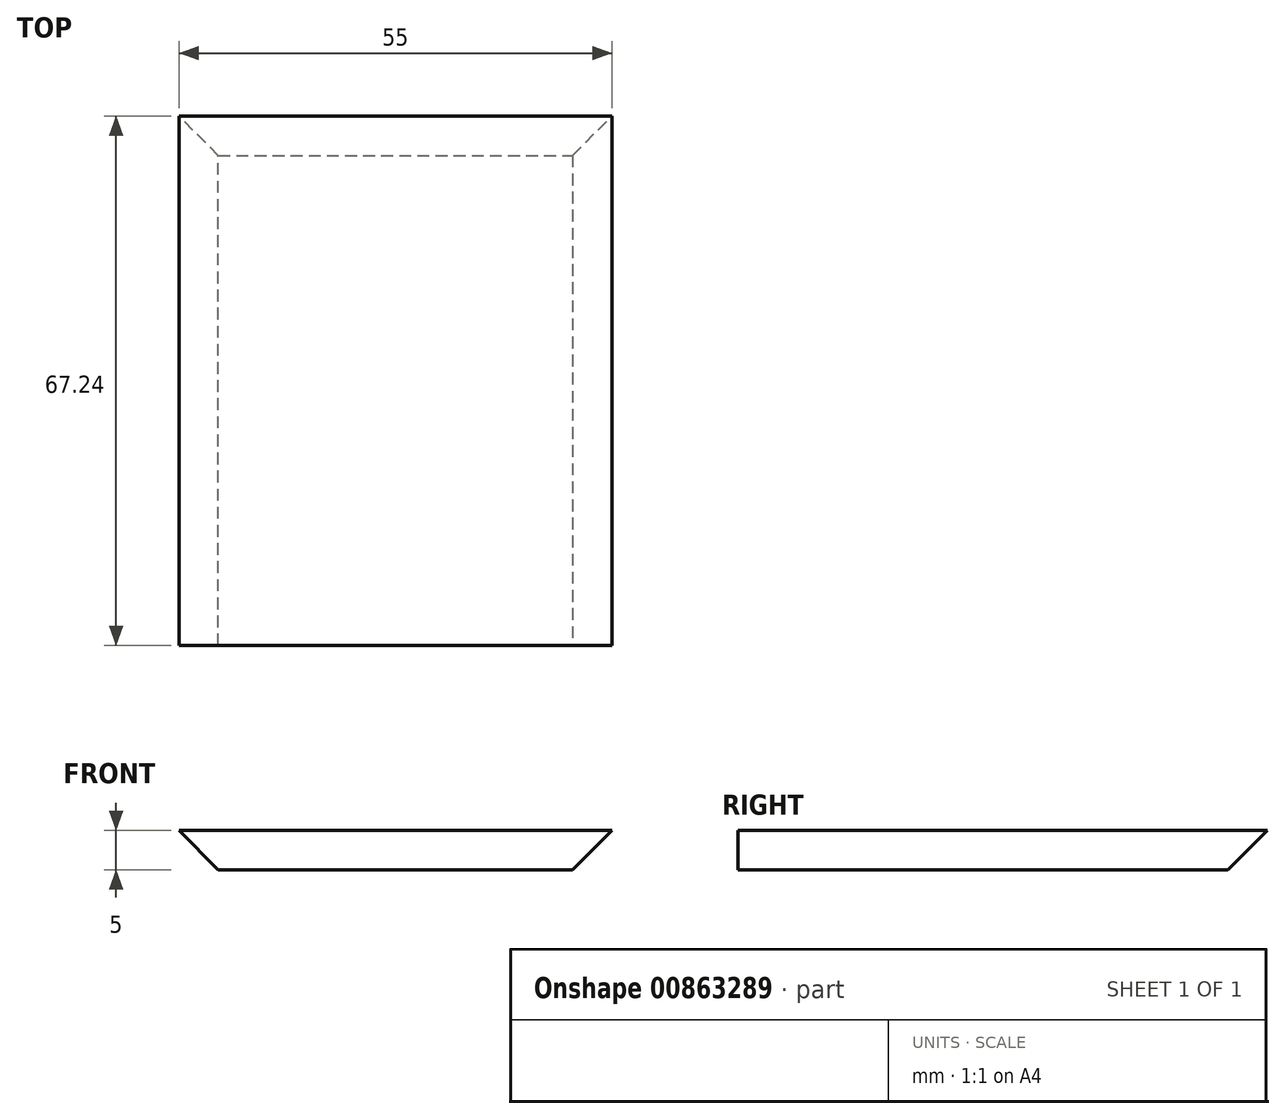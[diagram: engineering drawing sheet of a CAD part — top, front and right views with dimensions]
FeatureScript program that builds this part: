
annotation { "Feature Type Name" : "Feature", "Feature Type Description" : "" }
export const myFeature = defineFeature(function(context is Context, id is Id, definition is map)
    precondition{}
    {
        {
            var Q0;
            Q0=qCreatedBy(makeId("Top.planeOp"),FACE);
            var sketch = newSketch(context, id + "F0", { "sketchPlane" : qUnion([Q0])});
            skLineSegment(sketch, "E0.bottom", {"start": v(27.5, -52.5) * mm, "end": v(-27.5, -52.5) * mm});
            skLineSegment(sketch, "E0.top", {"start": v(27.5, 52.5) * mm, "end": v(-27.5, 52.5) * mm});
            skLineSegment(sketch, "E0.left", {"start": v(27.5, -52.5) * mm, "end": v(27.5, 52.5) * mm});
            skLineSegment(sketch, "E0.right", {"start": v(-27.5, -52.5) * mm, "end": v(-27.5, 52.5) * mm});
            skPoint(sketch, "E0.middle", {"position": v(0, 0) * mm});
            skLineSegment(sketch, "E1", {"start": v(27.5, -14.74) * mm, "end": v(-27.5, -11.5) * mm});
            skLineSegment(sketch, "E2", {"start": v(27.5, -14.74) * mm, "end": v(-27.5, -14.74) * mm});
            skSolve(sketch);
        }
        {
            var Q0;
            {var subQ0=sQuery(id+"F0.wireOp",EDGE,"E0.top");Q0=makeQuery(id+"F0.imprint","IMPRINT",FACE,{"disambiguationData":[TD([[makeQuery(id+"F0.imprint","IMPRINT",EDGE,{"derivedFrom":subQ0}),1.0]])]});}
            var Q1;
            {var subQ0=sQuery(id+"F0.wireOp",EDGE,"E1");Q1=makeQuery(id+"F0.imprint","IMPRINT",FACE,{"disambiguationData":[TD([[makeQuery(id+"F0.imprint","IMPRINT",EDGE,{"derivedFrom":subQ0}),1.0]])]});}
            extrude(context, id + "F1", {"entities" : qUnion([Q0, Q1]), "depth" : 5 * mm, "offsetDistance" : 25 * mm});
        }
        {
            var Q0;
            Q0=makeQuery(id+"F1.opExtrude","CAP_EDGE",EDGE,{"disambiguationData":[OSD([sQuery(id+"F0.wireOp",EDGE,"E0.left")])],"isStart":true});
            var Q1;
            Q1=makeQuery(id+"F1.opExtrude","CAP_EDGE",EDGE,{"disambiguationData":[OSD([sQuery(id+"F0.wireOp",EDGE,"E0.top")])],"isStart":true});
            var Q2;
            Q2=makeQuery(id+"F1.opExtrude","CAP_EDGE",EDGE,{"disambiguationData":[OSD([sQuery(id+"F0.wireOp",EDGE,"E0.right")])],"isStart":true});
            chamfer(context, id + "F2", {"entities" : qUnion([Q0, Q1, Q2]), "width" : 5 * mm, "tangentPropagation" : true});
        }
    });
